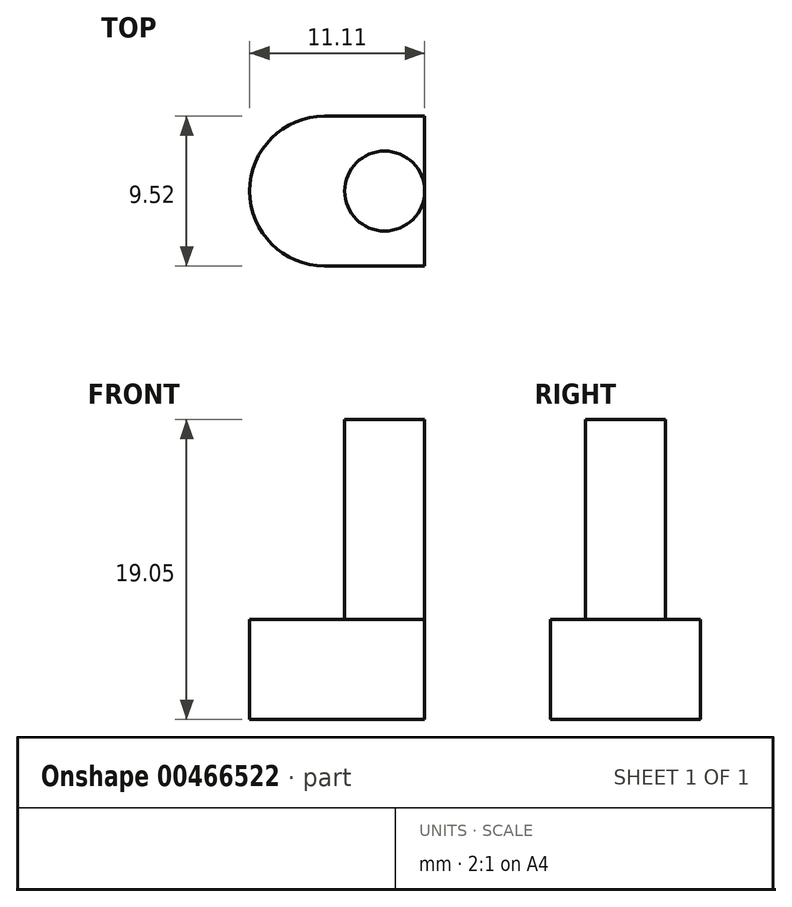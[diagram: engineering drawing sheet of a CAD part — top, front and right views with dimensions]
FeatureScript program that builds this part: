
annotation { "Feature Type Name" : "Feature", "Feature Type Description" : "" }
export const myFeature = defineFeature(function(context is Context, id is Id, definition is map)
    precondition{}
    {
        {
            var Q0;
            Q0=qCreatedBy(makeId("Top.planeOp"),FACE);
            var sketch = newSketch(context, id + "F0", { "sketchPlane" : qUnion([Q0])});
            skLineSegment(sketch, "E0.bottom", {"start": v(0, 4.76) * mm, "end": v(6.35, 4.76) * mm});
            skLineSegment(sketch, "E0.top", {"start": v(0, -4.76) * mm, "end": v(6.35, -4.76) * mm});
            skLineSegment(sketch, "E0.right", {"start": v(6.35, 4.76) * mm, "end": v(6.35, -4.76) * mm});
            skArc(sketch, "E1", {"start": v(0, -4.76) * mm, "mid": v(-4.76, 0) * mm, "end": v(0, 4.76) * mm});
            skSolve(sketch);
        }
        {
            var Q0;
            Q0=qCreatedBy(makeId("Top.planeOp"),FACE);
            var sketch = newSketch(context, id + "F1", { "sketchPlane" : qUnion([Q0])});
            skCircle(sketch, "E2", {"center": v(3.81, 0) * mm, "radius": 2.54 * mm});
            skSolve(sketch);
        }
        {
            var Q0;
            Q0=makeQuery(id+"F0.imprint","IMPRINT",FACE,{"disambiguationData":[TD([[makeQuery(id+"F0.imprint","IMPRINT",EDGE,{"derivedFrom":sQuery(id+"F0.wireOp",EDGE,"E0.bottom")}),-1.0]])]});
            extrude(context, id + "F2", {"entities" : qUnion([Q0]), "depth" : 6.35 * mm});
        }
        {
            var Q0;
            Q0=makeQuery(id+"F1.imprint","IMPRINT",FACE,{"disambiguationData":[TD([[makeQuery(id+"F1.imprint","IMPRINT",EDGE,{"derivedFrom":sQuery(id+"F1.wireOp",EDGE,"E2")}),1.0]])]});
            var Q1;
            Q1=sQuery(id+"F1.wireOp",EDGE,"E2");
            extrude(context, id + "F3", {"entities" : qUnion([Q0]), "operationType" : NewBodyOperationType.ADD, "surfaceEntities" : qUnion([Q1]), "depth" : 19.05 * mm});
        }
    });
